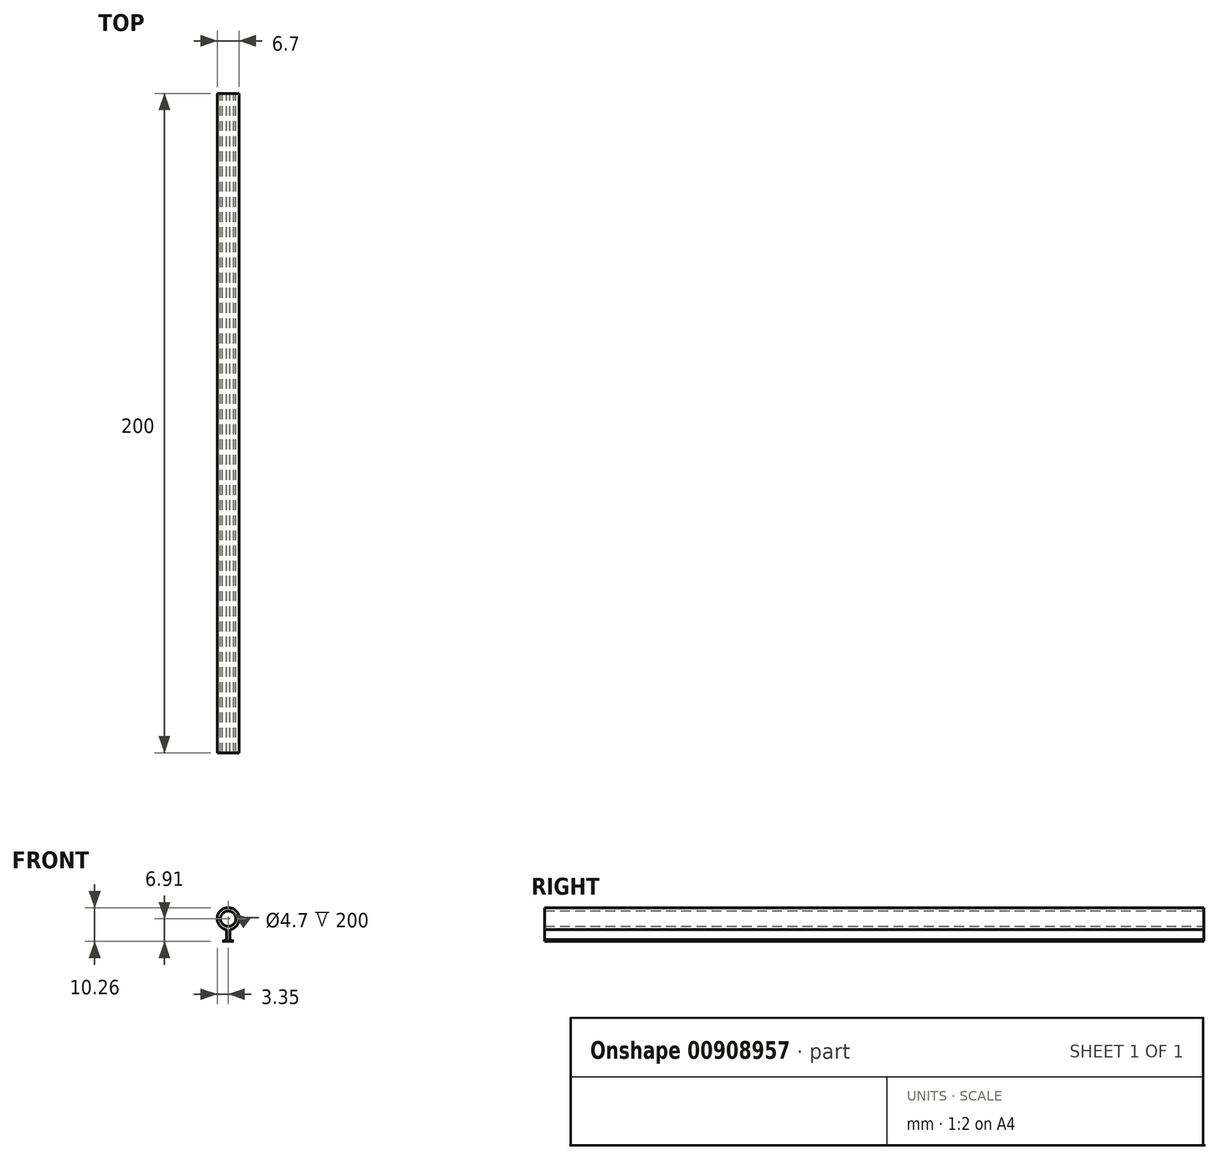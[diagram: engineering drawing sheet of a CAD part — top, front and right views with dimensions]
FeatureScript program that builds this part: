
annotation { "Feature Type Name" : "Feature", "Feature Type Description" : "" }
export const myFeature = defineFeature(function(context is Context, id is Id, definition is map)
    precondition{}
    {
        {
            var Q0;
            Q0=qCreatedBy(makeId("Front.planeOp"),FACE);
            var sketch = newSketch(context, id + "F0", { "sketchPlane" : qUnion([Q0])});
            skCircle(sketch, "E0", {"center": v(0, 0) * mm, "radius": 2.35 * mm});
            skCircle(sketch, "E1", {"center": v(0, 0) * mm, "radius": 3.35 * mm});
            skLineSegment(sketch, "E2.bottom", {"start": v(-0.5, -3.31) * mm, "end": v(0.5, -3.31) * mm});
            skLineSegment(sketch, "E2.top", {"start": v(-0.5, -6.31) * mm, "end": v(0.5, -6.31) * mm});
            skLineSegment(sketch, "E2.left", {"start": v(-0.5, -3.31) * mm, "end": v(-0.5, -6.31) * mm});
            skLineSegment(sketch, "E2.right", {"start": v(0.5, -3.31) * mm, "end": v(0.5, -6.31) * mm});
            skLineSegment(sketch, "E3", {"start": v(-0.5, -6.31) * mm, "end": v(-1.7, -6.91) * mm});
            skLineSegment(sketch, "E4", {"start": v(-1.7, -6.91) * mm, "end": v(1.63, -6.91) * mm});
            skLineSegment(sketch, "E5", {"start": v(1.63, -6.91) * mm, "end": v(0.5, -6.31) * mm});
            skSolve(sketch);
        }
        {
            var Q0;
            Q0=makeQuery(id+"F0.imprint","IMPRINT",FACE,{"disambiguationData":[TD([[makeQuery(id+"F0.imprint","IMPRINT",EDGE,{"derivedFrom":sQuery(id+"F0.wireOp",EDGE,"E2.top")}),1.0]])]});
            var Q1;
            {var subQ0=sQuery(id+"F0.wireOp",EDGE,"E2.bottom");Q1=makeQuery(id+"F0.imprint","IMPRINT",FACE,{"disambiguationData":[TD([[makeQuery(id+"F0.imprint","IMPRINT",EDGE,{"derivedFrom":subQ0}),-1.0]])]});}
            var Q2;
            Q2=makeQuery(id+"F0.imprint","IMPRINT",FACE,{"disambiguationData":[TD([[makeQuery(id+"F0.imprint","IMPRINT",EDGE,{"derivedFrom":sQuery(id+"F0.wireOp",EDGE,"E0")}),-1.0]])]});
            var Q3;
            Q3=makeQuery(id+"F0.imprint","IMPRINT",FACE,{"disambiguationData":[TD([[makeQuery(id+"F0.imprint","IMPRINT",EDGE,{"derivedFrom":sQuery(id+"F0.wireOp",EDGE,"E2.top")}),-1.0]])]});
            extrude(context, id + "F1", {"entities" : qUnion([Q0, Q1, Q2, Q3]), "depth" : 200 * mm, "offsetDistance" : 25 * mm});
        }
    });
